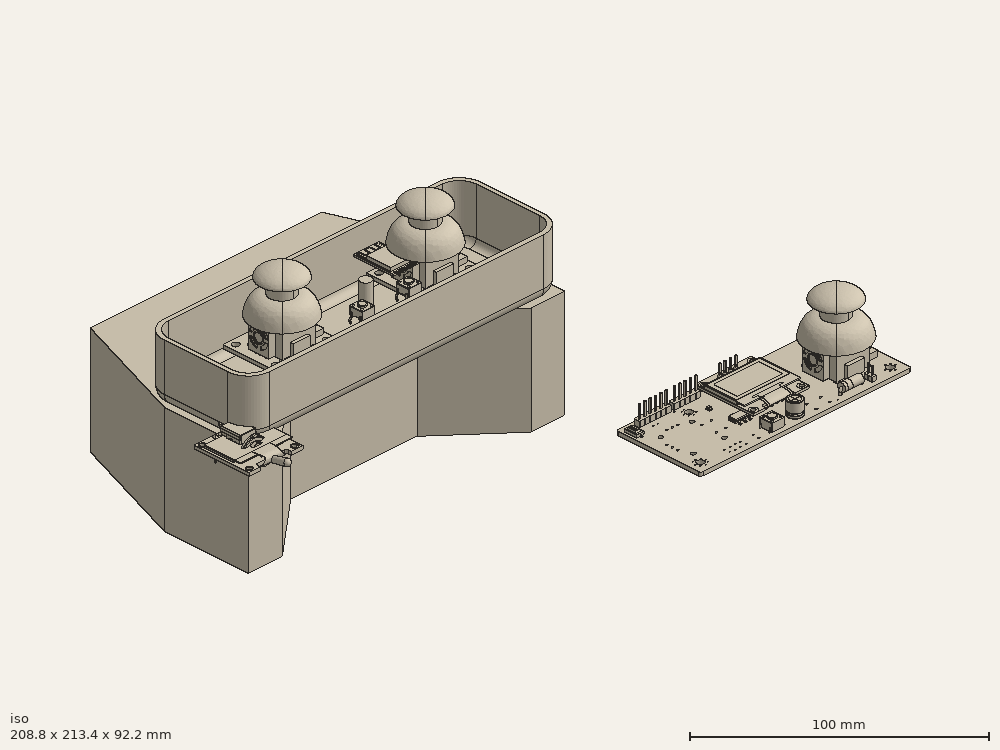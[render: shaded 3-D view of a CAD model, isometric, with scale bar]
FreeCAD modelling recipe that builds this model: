
FCSTD DOCUMENT  (FreeCAD 0.19R24366 (Git))
Label: Transmitter Case V1
License: All rights reserved
LicenseURL: http://en.wikipedia.org/wiki/All_rights_reserved
objects: Part::Feature×58, App::Link×30, Sketcher::SketchObject×13, App::Part×13, PartDesign::Pad×5, PartDesign::Body×5, PartDesign::Pocket×2, Mesh::Feature×1, PartDesign::Fillet×1, PartDesign::Thickness×1, PartDesign::CoordinateSystem×1
note: 95 computed .brp shape members not serialized (recipe doc carries the construction recipe); baked Part::Feature solids carry a one-line shape summary decoded from their .brp

FEATURE [Mesh::Feature] Xbox_One_Backplate_Electronic
  Placement = pos=(46,66,1.28e-14) rot=(1,0,0;3.14159rad)
FEATURE [Sketcher::SketchObject] Sketch
  FullyConstrained = true
  MapMode = 5
  Support = -> [XY_Plane]
  sketch-geometry (14):
    g0: LineSegment StartX=0 StartY=0 StartZ=0 EndX=0 EndY=40 EndZ=0
    g1: LineSegment StartX=0 StartY=40 StartZ=0 EndX=20 EndY=95 EndZ=0
    g2: LineSegment StartX=20 StartY=95 StartZ=0 EndX=130 EndY=95 EndZ=0
    g3: LineSegment StartX=130 StartY=95 StartZ=0 EndX=150 EndY=40 EndZ=0
    g4: LineSegment StartX=150 StartY=40 StartZ=0 EndX=150 EndY=0 EndZ=0
    g5: LineSegment StartX=150 StartY=0 StartZ=0 EndX=134 EndY=0 EndZ=0
    g6: LineSegment StartX=134 StartY=0 StartZ=0 EndX=105 EndY=25 EndZ=0
    g7: LineSegment StartX=105 StartY=25 StartZ=0 EndX=45 EndY=25 EndZ=0
    g8: LineSegment StartX=45 StartY=25 StartZ=0 EndX=16 EndY=0 EndZ=0
    g9: LineSegment StartX=16 StartY=0 StartZ=0 EndX=0 EndY=0 EndZ=0
    g10: LineSegment StartX=0 StartY=40 StartZ=0 EndX=20 EndY=40 EndZ=0
    g11: LineSegment StartX=150 StartY=40 StartZ=0 EndX=130 EndY=40 EndZ=0
    g12: LineSegment StartX=134 StartY=0 StartZ=0 EndX=105 EndY=0 EndZ=0
    g13: LineSegment StartX=16 StartY=0 StartZ=0 EndX=45 EndY=0 EndZ=0
  constraints (41):
    c: Coincident(g0,g-1)
    c: PointOnObject(g0,g-2)
    c: Coincident(g1,g0)
    c: Horizontal(g2)
    c: Coincident(g4,g3)
    c: Vertical(g4)
    c: Horizontal(g5)
    c: Coincident(g6,g5)
    c: Coincident(g7,g6)
    c: Horizontal(g7)
    c: Coincident(g8,g7)
    c: PointOnObject(g8,g-1)
    c: Coincident(g9,g8)
    c: Coincident(g9,g0)
    c: PointOnObject(g5,g-1)
    c: Equal(g0,g4)
    c: Equal(g8,g6)
    c: Equal(g9,g5)
    c: Equal(g1,g3)
    c: Coincident(g10,g0)
    c: Horizontal(g10)
    c: Coincident(g11,g3)
    c: Horizontal(g11)
    c: Coincident(g12,g5)
    c: Coincident(g13,g8)
    c: Horizontal(g13)
    c: Horizontal(g12)
    c: Vertical(g13,g7)
    c: Vertical(g12,g6)
    c: Distance(g7) = 60
    c: Distance(g3,g1) = 110
    c: Equal(g10,g11)
    c: DistanceY(g0,g2) = 95
    c: Distance(g0,g5) = 150
    c: Coincident(g1,g2)
    c: Coincident(g2,g3)
    c: Vertical(g11,g2)
    c: Coincident(g5,g4)
    c: Distance(g4) = 40
    c: Distance(g5) = 16
    c: Distance(g7,g13) = 25
FEATURE [PartDesign::Pad] Pad
  Direction = (1,1,1)
  Length = 48
  Length2 = 100
  Profile = -> Sketch
  Reversed = true
  Type = 0
FEATURE [Sketcher::SketchObject] Sketch001
  ExternalGeometry = -> [Pad]
  FullyConstrained = true
  MapMode = 5
  Support = -> [Pad]
  sketch-geometry (4):
    g0: LineSegment StartX=0 StartY=-1 StartZ=0 EndX=-63.05 EndY=-1 EndZ=0
    g1: LineSegment StartX=-63.05 StartY=-1 StartZ=0 EndX=-63.05 EndY=98.76 EndZ=0
    g2: LineSegment StartX=-63.05 StartY=98.76 StartZ=0 EndX=0 EndY=98.76 EndZ=0
    g3: LineSegment StartX=0 StartY=98.76 StartZ=0 EndX=0 EndY=-1 EndZ=0
  constraints (12):
    c: Coincident(g0,g1)
    c: Coincident(g1,g2)
    c: Coincident(g2,g3)
    c: Coincident(g3,g0)
    c: Horizontal(g0)
    c: Horizontal(g2)
    c: Vertical(g1)
    c: Vertical(g3)
    c: Distance(g0) = 63.05
    c: Distance(g3) = 99.76
    c: Vertical(g-1,g0)
    c: Distance(g-1,g0) = 1
FEATURE [PartDesign::Body] Body
  Group = -> [Sketch,Pad,Sketch001]
  Origin = -> Origin
  Tip = -> Pad
FEATURE [Sketcher::SketchObject] Sketch002
  FullyConstrained = true
  MapMode = 5
  Support = -> [XY_Plane001]
  sketch-geometry (16):
    g0: LineSegment StartX=10 StartY=0 StartZ=0 EndX=140 EndY=0 EndZ=0
    g1: LineSegment StartX=150 StartY=10 StartZ=0 EndX=150 EndY=40 EndZ=0
    g2: LineSegment StartX=140 StartY=50 StartZ=0 EndX=10 EndY=50 EndZ=0
    g3: LineSegment StartX=0 StartY=40 StartZ=0 EndX=0 EndY=10 EndZ=0
    g4: LineSegment StartX=0 StartY=0 StartZ=0 EndX=150 EndY=0 EndZ=0
    g5: LineSegment StartX=150 StartY=0 StartZ=0 EndX=150 EndY=50 EndZ=0
    g6: LineSegment StartX=150 StartY=50 StartZ=0 EndX=0 EndY=50 EndZ=0
    g7: LineSegment StartX=0 StartY=50 StartZ=0 EndX=0 EndY=0 EndZ=0
    g8: ArcOfCircle CenterX=140 CenterY=40 CenterZ=0 NormalX=0 NormalY=0 NormalZ=1 AngleXU=0 Radius=10 StartAngle=2e-16 EndAngle=1.5708
    g9: ArcOfCircle CenterX=140 CenterY=10 CenterZ=0 NormalX=0 NormalY=0 NormalZ=1 AngleXU=0 Radius=10 StartAngle=4.71239 EndAngle=6.28319
    g10: ArcOfCircle CenterX=10 CenterY=10 CenterZ=0 NormalX=0 NormalY=0 NormalZ=1 AngleXU=0 Radius=10 StartAngle=3.14159 EndAngle=4.71239
    g11: ArcOfCircle CenterX=10 CenterY=40 CenterZ=0 NormalX=0 NormalY=0 NormalZ=1 AngleXU=0 Radius=10 StartAngle=1.5708 EndAngle=3.14159
    g12: LineSegment StartX=140 StartY=40 StartZ=0 EndX=140 EndY=50 EndZ=0
    g13: LineSegment StartX=140 StartY=10 StartZ=0 EndX=140 EndY=0 EndZ=0
    g14: LineSegment StartX=10 StartY=0 StartZ=0 EndX=10 EndY=10 EndZ=0
    g15: LineSegment StartX=10 StartY=40 StartZ=0 EndX=10 EndY=50 EndZ=0
  constraints (39):
    c: Horizontal(g0)
    c: Vertical(g1)
    c: Vertical(g3)
    c: Coincident(g4,g5)
    c: Coincident(g5,g6)
    c: Coincident(g6,g7)
    c: Coincident(g7,g4)
    c: Horizontal(g4)
    c: Horizontal(g6)
    c: Vertical(g5)
    c: Vertical(g7)
    c: Coincident(g4,g-1)
    c: Distance(g5) = 50
    c: Distance(g4) = 150
    c: Tangent(g2,g8) = -1.5708
    c: Tangent(g1,g8) = -1.5708
    c: Tangent(g1,g9) = -1.5708
    c: Tangent(g0,g9) = -1.5708
    c: Tangent(g0,g10) = -1.5708
    c: Tangent(g3,g10) = -1.5708
    c: Tangent(g2,g11) = -1.5708
    c: Tangent(g3,g11) = -1.5708
    c: PointOnObject(g0,g4)
    c: PointOnObject(g3,g7)
    c: PointOnObject(g2,g6)
    c: PointOnObject(g1,g5)
    c: Coincident(g12,g8)
    c: Coincident(g12,g2)
    c: Vertical(g12)
    c: Coincident(g13,g9)
    c: Coincident(g13,g0)
    c: Coincident(g14,g0)
    c: Coincident(g14,g10)
    c: Coincident(g15,g11)
    c: Coincident(g15,g2)
    c: Equal(g15,g14)
    c: Equal(g14,g12)
    c: Equal(g12,g13)
    c: Distance(g15) = 10
FEATURE [PartDesign::Pad] Pad001
  Direction = (1,1,1)
  Length = 26
  Length2 = 100
  Profile = -> Sketch002
  Type = 0
FEATURE [PartDesign::Fillet] Fillet
  Base = -> Pad001 [Edge3]
  BaseFeature = -> Pad001
  Radius = 5
  SupportTransform = false
FEATURE [PartDesign::Thickness] Thickness
  Base = -> Fillet [Face4]
  BaseFeature = -> Fillet
  Intersection = false
  Join = 0
  Mode = 0
  Reversed = true
  SupportTransform = false
  Value = 2
FEATURE [Part::Feature] Part__Feature  label="9032"
  Placement = pos=(101,33,14) rot=(0,0,-1;1.5708rad)
  shape: bbox 56.58 x 56.58 x 34.67 mm, 175 faces (baked)
FEATURE [Part::Feature] Part__Feature001  label="9032001"
  Placement = pos=(33,33,14) rot=(0,0,-1;1.5708rad)
  shape: bbox 56.58 x 56.58 x 34.67 mm, 175 faces (baked)
FEATURE [Part::Feature] Part__Feature002  label="board"
  shape: bbox 25.4 x 26.2 x 1.51 mm, 314 faces, 9 solids (baked)
FEATURE [Part::Feature] Part__Feature003  label="screen"
  shape: bbox 24.7 x 17 x 1.8 mm, 20 faces, 3 solids (baked)
FEATURE [Part::Feature] Part__Feature004  label="pin_header"
  shape: bbox 10.16 x 2.54 x 11 mm, 112 faces, 8 solids (baked)
FEATURE [Part::Feature] Part__Feature005  label="soldering"
  shape: bbox 9.839 x 2.219 x 0.9038 mm, 24 faces, 4 solids (baked)
FEATURE [Part::Feature] Part__Feature006  label="smd_capacitor"
  Placement = pos=(10.775,1.3,0) rot=(1,0,0;3.14159rad)
  shape: bbox 0.85 x 1.6 x 0.8 mm, 18 faces, 3 solids (baked)
FEATURE [Part::Feature] Part__Feature007  label="smd_capacitor (1)"
  Placement = pos=(9.275,1.3,0) rot=(1,0,0;3.14159rad)
  shape: bbox 0.85 x 1.6 x 0.8 mm, 18 faces, 3 solids (baked)
FEATURE [Part::Feature] Part__Feature008  label="914_smd_resistor"
  Placement = pos=(7.775,1.3,0) rot=(1,0,0;3.14159rad)
  shape: bbox 0.85 x 1.55 x 0.46 mm, 76 faces, 3 solids (baked)
FEATURE [Part::Feature] Part__Feature009  label="472_smd_resistor"
  Placement = pos=(6.275,1.3,0) rot=(1,0,0;3.14159rad)
  shape: bbox 0.85 x 1.55 x 0.46 mm, 69 faces, 3 solids (baked)
FEATURE [Part::Feature] Part__Feature010  label="472_smd_resistor001"
  Placement = pos=(4.775,1.3,0) rot=(1,0,0;3.14159rad)
  shape: bbox 0.85 x 1.55 x 0.46 mm, 69 faces, 3 solids (baked)
FEATURE [Part::Feature] Part__Feature011  label="472_smd_resistor002"
  Placement = pos=(3.275,1.3,0) rot=(1,0,0;3.14159rad)
  shape: bbox 0.85 x 1.55 x 0.46 mm, 69 faces, 3 solids (baked)
FEATURE [Part::Feature] Part__Feature012  label="t4_smd_diode"
  Placement = pos=(1.375,1.3,-0.19) rot=(1,0,0;3.14159rad)
  shape: bbox 1.272 x 2.502 x 1.002 mm, 51 faces, 3 solids (baked)
FEATURE [Part::Feature] Part__Feature013  label="smd_capacitor (2)"
  Placement = pos=(-0.225,1.3,0) rot=(1,0,0;3.14159rad)
  shape: bbox 0.85 x 1.6 x 0.8 mm, 18 faces, 3 solids (baked)
FEATURE [Part::Feature] Part__Feature014  label="smd_capacitor (3)"
  Placement = pos=(-3.725,1.3,0) rot=(1,0,0;3.14159rad)
  shape: bbox 0.85 x 1.6 x 0.8 mm, 18 faces, 3 solids (baked)
FEATURE [Part::Feature] Part__Feature015  label="smd_capacitor (4)"
  Placement = pos=(-5.225,1.3,0) rot=(1,0,0;3.14159rad)
  shape: bbox 0.85 x 1.6 x 0.8 mm, 18 faces, 3 solids (baked)
FEATURE [Part::Feature] Part__Feature016  label="smd_capacitor (5)"
  Placement = pos=(-7.725,1.3,0) rot=(1,0,0;3.14159rad)
  shape: bbox 0.85 x 1.6 x 0.8 mm, 18 faces, 3 solids (baked)
FEATURE [Part::Feature] Part__Feature017  label="smd_capacitor (6)"
  Placement = pos=(-9.225,1.3,0) rot=(1,0,0;3.14159rad)
  shape: bbox 0.85 x 1.6 x 0.8 mm, 18 faces, 3 solids (baked)
FEATURE [Part::Feature] Part__Feature018  label="472_smd_resistor (1)"
  Placement = pos=(6.925,6.675,0) rot=(0.707107,-0.707107,0;3.14159rad)
  shape: bbox 1.55 x 0.85 x 0.46 mm, 69 faces, 3 solids (baked)
FEATURE [Part::Feature] Part__Feature019  label="SOT-23_XC6206 v3"
  Placement = pos=(-0.75,7.3,-0.1) rot=(0.707107,-0.707107,0;3.14159rad)
  shape: bbox 2.9 x 2.8 x 1.21 mm, 135 faces, 4 solids (baked)
FEATURE [Part::Feature] Part__Feature020  label="smd_capacitor (7)"
  Placement = pos=(-4,7.3,-0.8) rot=(0,0,1;0rad)
  shape: bbox 0.85 x 1.6 x 0.8 mm, 18 faces, 3 solids (baked)
FEATURE [Part::Feature] Part__Feature021  label="flat_cable"
  shape: bbox 22 x 8.057 x 3.352 mm, 10 faces (baked)
FEATURE [App::Part] SSD1306_OLED_Display_128x64__v23  label="SSD1306_OLED_Display(128x64) v23"
  Group = -> [Part__Feature002,Part__Feature003,Part__Feature004,Part__Feature005,Part__Feature006,Part__Feature007,Part__Feature008,Part__Feature009,Part__Feature010,Part__Feature011,Part__Feature012,Part__Feature013,Part__Feature014,Part__Feature015,Part__Feature016,Part__Feature017,Part__Feature018,Part__Feature019,Part__Feature020,Part__Feature021]
  Origin = -> Origin002
  Placement = pos=(75,30,24) rot=(0,0,1;0rad)
FEATURE [Part::Feature] Part__Feature022  label="COMPOUND"
  shape: bbox 12 x 9.988 x 12.9 mm, 195 faces, 5 solids (baked)
FEATURE [App::Part] MTS_1xx_Base_TH  label="MTS-1xx-Base_TH"
  Group = -> [Part__Feature022]
  Origin = -> Origin003
FEATURE [Part::Feature] Part__Feature024  label="MTS-1xx-Handle"
  Placement = pos=(0,-8.8,0) rot=(0,0,1;0rad)
  shape: bbox 3.8 x 17.38 x 5.93 mm, 7 faces (baked)
FEATURE [Part::Feature] Part__Feature025  label="MTS-1xx-Contact"
  Placement = pos=(0,5.9,0) rot=(0,0,1;0rad)
  shape: bbox 3.55 x 1.359 x 10.22 mm, 24 faces (baked)
FEATURE [Part::Feature] Part__Feature026  label="COMPOUND002"
  shape: bbox 3.55 x 20.58 x 3.55 mm, 13 faces, 3 solids (baked)
FEATURE [Part::Feature] Part__Feature027  label="COMPOUND003"
  shape: bbox 1.101 x 7.18 x 1.101 mm, 0 faces, 0 solids (baked)
FEATURE [App::Part] MTS_1xx_Pin  label="MTS-1xx-Pin"
  Group = -> [Part__Feature026,Part__Feature027]
  Origin = -> Origin004
  Placement = pos=(0,-7.39942,0.106156) rot=(-1,0,0;0.20944rad)
FEATURE [Part::Feature] Part__Feature028  label="MTS-1xx-Terminal1"
  Placement = pos=(0,5.9,0) rot=(0,0,1;0rad)
  shape: bbox 3.7 x 7.6 x 10.2 mm, 84 faces, 3 solids (baked)
FEATURE [Part::Feature] Part__Feature029  label="MTS-1xx-Housing"
  shape: bbox 7.9 x 10.3 x 13.2 mm, 921 faces, 2 solids (baked)
FEATURE [App::Part] MTS_1xx_X1  label="MTS-1xx-X1"
  Group = -> [MTS_1xx_Base_TH,Part__Feature024,Part__Feature025,MTS_1xx_Pin,Part__Feature028,Part__Feature029]
  Origin = -> Origin005
  Placement = pos=(16,42,17) rot=(0,0,-1;3.14159rad)
FEATURE [Part::Feature] Part__Feature030  label="MTS-1xx-Contact001"
  Placement = pos=(0,5.9,0) rot=(0,0,1;0rad)
  shape: bbox 3.55 x 1.359 x 10.22 mm, 24 faces (baked)
FEATURE [Part::Feature] Part__Feature031  label="MTS-1xx-Handle001"
  Placement = pos=(0,-8.8,0) rot=(0,0,1;0rad)
  shape: bbox 3.8 x 17.38 x 5.93 mm, 7 faces (baked)
FEATURE [Part::Feature] Part__Feature032  label="COMPOUND004"
  shape: bbox 3.55 x 20.58 x 3.55 mm, 13 faces, 3 solids (baked)
FEATURE [Part::Feature] Part__Feature033  label="COMPOUND005"
  shape: bbox 1.101 x 7.18 x 1.101 mm, 0 faces, 0 solids (baked)
FEATURE [App::Part] MTS_1xx_Pin001  label="MTS-1xx-Pin001"
  Group = -> [Part__Feature032,Part__Feature033]
  Origin = -> Origin007
  Placement = pos=(0,-7.39942,0.106156) rot=(-1,0,0;0.20944rad)
FEATURE [Part::Feature] Part__Feature034  label="COMPOUND006"
  shape: bbox 12 x 9.988 x 12.9 mm, 195 faces, 5 solids (baked)
FEATURE [App::Part] MTS_1xx_Base_TH001  label="MTS-1xx-Base_TH001"
  Group = -> [Part__Feature034]
  Origin = -> Origin008
FEATURE [Part::Feature] Part__Feature035  label="MTS-1xx-Terminal002"
  Placement = pos=(0,5.9,0) rot=(0,0,1;0rad)
  shape: bbox 3.7 x 7.6 x 10.2 mm, 84 faces, 3 solids (baked)
FEATURE [Part::Feature] Part__Feature036  label="MTS-1xx-Housing001"
  shape: bbox 7.9 x 10.3 x 13.2 mm, 921 faces, 2 solids (baked)
FEATURE [App::Part] MTS_1xx_X002  label="MTS-1xx-X002"
  Group = -> [MTS_1xx_Base_TH001,Part__Feature031,Part__Feature030,MTS_1xx_Pin001,Part__Feature035,Part__Feature036]
  Origin = -> Origin006
  Placement = pos=(134,42,17) rot=(0,0,-1;3.14159rad)
FEATURE [Part::Feature] Part__Feature037  label="Tactile Switch 6mm - THT"
  Placement = pos=(64,10,22) rot=(0,0,1;0rad)
  shape: bbox 7.902 x 6.002 x 7.802 mm, 138 faces, 7 solids (baked)
FEATURE [Sketcher::SketchObject] Sketch003
  FullyConstrained = true
  MapMode = 5
  Support = -> [XY_Plane009]
  sketch-geometry (40):
    g0: LineSegment StartX=0 StartY=0 StartZ=0 EndX=30 EndY=0 EndZ=0
    g1: LineSegment StartX=30 StartY=0 StartZ=0 EndX=30 EndY=25 EndZ=0
    g2: LineSegment StartX=30 StartY=25 StartZ=0 EndX=0 EndY=25 EndZ=0
    g3: LineSegment StartX=0 StartY=25 StartZ=0 EndX=0 EndY=0 EndZ=0
    g4: Circle CenterX=4.4 CenterY=8.5 CenterZ=0 NormalX=0 NormalY=0 NormalZ=1 AngleXU=0 Radius=0.75
    g5: Circle CenterX=4.4 CenterY=11.05 CenterZ=0 NormalX=0 NormalY=0 NormalZ=1 AngleXU=0 Radius=0.75
    g6: Circle CenterX=4.4 CenterY=13.6 CenterZ=0 NormalX=0 NormalY=0 NormalZ=1 AngleXU=0 Radius=0.75
    g7: Circle CenterX=11.4 CenterY=20.6 CenterZ=0 NormalX=0 NormalY=0 NormalZ=1 AngleXU=0 Radius=0.75
    g8: Circle CenterX=13.95 CenterY=20.6 CenterZ=0 NormalX=0 NormalY=0 NormalZ=1 AngleXU=0 Radius=0.75
    g9: Circle CenterX=16.5 CenterY=20.6 CenterZ=0 NormalX=0 NormalY=0 NormalZ=1 AngleXU=0 Radius=0.75
    g10: Circle CenterX=26.4 CenterY=14.65 CenterZ=0 NormalX=0 NormalY=0 NormalZ=1 AngleXU=0 Radius=0.75
    g11: Circle CenterX=26.4 CenterY=7.8 CenterZ=0 NormalX=0 NormalY=0 NormalZ=1 AngleXU=0 Radius=0.75
    g12: Circle CenterX=22.1 CenterY=7.8 CenterZ=0 NormalX=0 NormalY=0 NormalZ=1 AngleXU=0 Radius=0.75
    g13: Circle CenterX=22.1 CenterY=14.65 CenterZ=0 NormalX=0 NormalY=0 NormalZ=1 AngleXU=0 Radius=0.75
    g14: Circle CenterX=6.5 CenterY=3.35 CenterZ=0 NormalX=0 NormalY=0 NormalZ=1 AngleXU=0 Radius=1
    g15: Circle CenterX=6.5 CenterY=18.75 CenterZ=0 NormalX=0 NormalY=0 NormalZ=1 AngleXU=0 Radius=1
    g16: Circle CenterX=21.35 CenterY=3.35 CenterZ=0 NormalX=0 NormalY=0 NormalZ=1 AngleXU=0 Radius=1
    g17: Circle CenterX=21.35 CenterY=18.75 CenterZ=0 NormalX=0 NormalY=0 NormalZ=1 AngleXU=0 Radius=1
    g18: LineSegment StartX=13.95 StartY=20.6 StartZ=0 EndX=13.95 EndY=25 EndZ=0
    g19: LineSegment StartX=16.5 StartY=20.6 StartZ=0 EndX=13.95 EndY=20.6 EndZ=0
    g20: LineSegment StartX=11.4 StartY=20.6 StartZ=0 EndX=13.95 EndY=20.6 EndZ=0
    g21: LineSegment StartX=13.95 StartY=20.6 StartZ=0 EndX=0 EndY=20.6 EndZ=0
    g22: LineSegment StartX=4.4 StartY=11.05 StartZ=0 EndX=0 EndY=11.05 EndZ=0
    g23: LineSegment StartX=4.4 StartY=13.6 StartZ=0 EndX=4.4 EndY=11.05 EndZ=0
    g24: LineSegment StartX=4.4 StartY=11.05 StartZ=0 EndX=4.4 EndY=8.5 EndZ=0
    g25: LineSegment StartX=4.4 StartY=11.05 StartZ=0 EndX=4.4 EndY=25 EndZ=0
    g26: LineSegment StartX=6.5 StartY=3.35 StartZ=0 EndX=0 EndY=3.35 EndZ=0
    g27: LineSegment StartX=6.5 StartY=3.35 StartZ=0 EndX=6.5 EndY=0 EndZ=0
    g28: LineSegment StartX=26.4 StartY=7.8 StartZ=0 EndX=26.4 EndY=0 EndZ=0
    g29: LineSegment StartX=26.4 StartY=7.8 StartZ=0 EndX=30 EndY=7.8 EndZ=0
    g30: LineSegment StartX=6.5 StartY=18.75 StartZ=0 EndX=6.5 EndY=25 EndZ=0
    g31: LineSegment StartX=6.5 StartY=18.75 StartZ=0 EndX=0 EndY=18.75 EndZ=0
    g32: LineSegment StartX=21.35 StartY=18.75 StartZ=0 EndX=21.35 EndY=25 EndZ=0
    g33: LineSegment StartX=21.35 StartY=18.75 StartZ=0 EndX=30 EndY=18.75 EndZ=0
    g34: LineSegment StartX=21.35 StartY=3.35 StartZ=0 EndX=21.35 EndY=0 EndZ=0
    g35: LineSegment StartX=21.35 StartY=3.35 StartZ=0 EndX=30 EndY=3.35 EndZ=0
    g36: LineSegment StartX=26.4 StartY=14.65 StartZ=0 EndX=26.4 EndY=7.8 EndZ=0
    g37: LineSegment StartX=26.4 StartY=7.8 StartZ=0 EndX=22.1 EndY=7.8 EndZ=0
    g38: LineSegment StartX=22.1 StartY=14.65 StartZ=0 EndX=22.1 EndY=7.8 EndZ=0
    g39: LineSegment StartX=26.4 StartY=14.65 StartZ=0 EndX=22.1 EndY=14.65 EndZ=0
  constraints (111):
    c: Coincident(g0,g1)
    c: Coincident(g1,g2)
    c: Coincident(g2,g3)
    c: Coincident(g3,g0)
    c: Horizontal(g0)
    c: Horizontal(g2)
    c: Vertical(g1)
    c: Vertical(g3)
    c: Coincident(g0,g-1)
    c: Distance(g2) = 30
    c: Distance(g1) = 25
    c: Diameter(g4) = 1.5
    c: Equal(g4,g5) = 1.5
    c: Equal(g4,g6) = 1.5
    c: Equal(g4,g7) = 1.5
    c: Equal(g4,g8) = 1.5
    c: Equal(g4,g9) = 1.5
    c: Equal(g4,g10) = 1.5
    c: Equal(g4,g11) = 1.5
    c: Equal(g4,g12) = 1.5
    c: Diameter(g14) = 2
    c: Equal(g14,g15) = 2
    c: Equal(g14,g16) = 2
    c: Equal(g14,g17) = 2
    c: Coincident(g18,g8)
    c: Vertical(g18)
    c: Coincident(g19,g9)
    c: Coincident(g19,g8)
    c: Horizontal(g19)
    c: Coincident(g20,g7)
    c: Coincident(g20,g8)
    c: Horizontal(g20)
    c: Equal(g20,g19)
    c: Distance(g18) = 4.4
    c: Coincident(g21,g8)
    c: PointOnObject(g21,g3)
    c: Horizontal(g21)
    c: PointOnObject(g18,g2)
    c: Distance(g21) = 13.95
    c: Distance(g20) = 2.55
    c: Coincident(g22,g5)
    c: PointOnObject(g22,g-2)
    c: Horizontal(g22)
    c: Coincident(g23,g6)
    c: Coincident(g23,g5)
    c: Vertical(g23)
    c: Coincident(g24,g5)
    c: Coincident(g24,g4)
    c: Vertical(g24)
    c: Equal(g24,g23)
    c: Distance(g22) = 4.4
    c: Coincident(g25,g5)
    c: PointOnObject(g25,g2)
    c: Vertical(g25)
    c: Distance(g25) = 13.95
    c: Distance(g24) = 2.55
    c: Coincident(g26,g14)
    c: PointOnObject(g26,g-2)
    c: Horizontal(g26)
    c: Coincident(g27,g14)
    c: PointOnObject(g27,g0)
    c: Vertical(g27)
    c: Coincident(g28,g11)
    c: PointOnObject(g28,g0)
    c: Vertical(g28)
    c: Coincident(g29,g11)
    c: Horizontal(g29)
    c: Coincident(g30,g15)
    c: PointOnObject(g30,g2)
    c: Vertical(g30)
    c: Coincident(g31,g15)
    c: PointOnObject(g31,g3)
    c: Horizontal(g31)
    c: Coincident(g32,g17)
    c: PointOnObject(g32,g2)
    c: Vertical(g32)
    c: Coincident(g33,g17)
    c: PointOnObject(g33,g1)
    c: Horizontal(g33)
    c: Coincident(g34,g16)
    c: PointOnObject(g34,g0)
    c: Vertical(g34)
    c: Coincident(g35,g16)
    c: PointOnObject(g35,g1)
    c: Horizontal(g35)
    c: Coincident(g36,g10)
    c: Coincident(g36,g11)
    c: Vertical(g36)
    c: Coincident(g37,g11)
    c: Coincident(g37,g12)
    c: Horizontal(g37)
    c: Coincident(g38,g13)
    c: Coincident(g38,g12)
    c: Vertical(g38)
    c: Coincident(g39,g10)
    c: Coincident(g39,g13)
    c: Horizontal(g39)
    c: Distance(g29) = 3.6
    c: Distance(g37) = 4.3
    c: Distance(g38) = 6.85
    c: Distance(g28) = 7.8
    c: PointOnObject(g29,g1)
    c: Equal(g13,g12)
    c: Distance(g31) = 6.5
    c: Distance(g30) = 6.25
    c: Distance(g32) = 6.25
    c: Distance(g33) = 8.65
    c: Distance(g35) = 8.65
    c: Distance(g34) = 3.35
    c: Distance(g27) = 3.35
    c: Distance(g26) = 6.5
FEATURE [PartDesign::Pad] Pad002
  Direction = (1,1,1)
  Length = 1.6
  Length2 = 100
  Profile = -> Sketch003
  Type = 0
FEATURE [Sketcher::SketchObject] Sketch004
  ExternalGeometry = -> [Pad002]
  FullyConstrained = true
  MapMode = 5
  Placement = pos=(0,0,1.6) rot=(0,0,1;0rad)
  Support = -> [Pad002]
  sketch-geometry (4):
    g0: Circle CenterX=27 CenterY=22 CenterZ=0 NormalX=0 NormalY=0 NormalZ=1 AngleXU=0 Radius=1.55
    g1: Circle CenterX=3 CenterY=22 CenterZ=0 NormalX=0 NormalY=0 NormalZ=1 AngleXU=0 Radius=1.55
    g2: Circle CenterX=27 CenterY=3 CenterZ=0 NormalX=0 NormalY=0 NormalZ=1 AngleXU=0 Radius=1.55
    g3: Circle CenterX=3 CenterY=3 CenterZ=0 NormalX=0 NormalY=0 NormalZ=1 AngleXU=0 Radius=1.55
  constraints (12):
    c: Diameter(g0) = 3.1
    c: Equal(g0,g1) = 3.1
    c: Equal(g0,g2) = 3.1
    c: Equal(g0,g3) = 3.1
    c: Distance(g2,g-5) = 3
    c: Distance(g2,g-6) = 3
    c: Distance(g0,g-3) = 3
    c: Distance(g0,g-5) = 3
    c: Distance(g1,g-3) = 3
    c: Distance(g1,g-4) = 3
    c: Distance(g3,g-4) = 3
    c: Distance(g3,g-6) = 3
FEATURE [PartDesign::Pocket] Pocket
  BaseFeature = -> Pad002
  Length = 5
  Length2 = 100
  Profile = -> Sketch004
  Type = 0
FEATURE [Sketcher::SketchObject] Sketch006
  FullyConstrained = true
  MapMode = 5
  Support = -> [XY_Plane010]
  sketch-geometry (40):
    g0: LineSegment StartX=0 StartY=0 StartZ=0 EndX=30 EndY=0 EndZ=0
    g1: LineSegment StartX=30 StartY=0 StartZ=0 EndX=30 EndY=25 EndZ=0
    g2: LineSegment StartX=30 StartY=25 StartZ=0 EndX=0 EndY=25 EndZ=0
    g3: LineSegment StartX=0 StartY=25 StartZ=0 EndX=0 EndY=0 EndZ=0
    g4: Circle CenterX=4.4 CenterY=8.5 CenterZ=0 NormalX=0 NormalY=0 NormalZ=1 AngleXU=0 Radius=0.75
    g5: Circle CenterX=4.4 CenterY=11.05 CenterZ=0 NormalX=0 NormalY=0 NormalZ=1 AngleXU=0 Radius=0.75
    g6: Circle CenterX=4.4 CenterY=13.6 CenterZ=0 NormalX=0 NormalY=0 NormalZ=1 AngleXU=0 Radius=0.75
    g7: Circle CenterX=11.4 CenterY=20.6 CenterZ=0 NormalX=0 NormalY=0 NormalZ=1 AngleXU=0 Radius=0.75
    g8: Circle CenterX=13.95 CenterY=20.6 CenterZ=0 NormalX=0 NormalY=0 NormalZ=1 AngleXU=0 Radius=0.75
    g9: Circle CenterX=16.5 CenterY=20.6 CenterZ=0 NormalX=0 NormalY=0 NormalZ=1 AngleXU=0 Radius=0.75
    g10: Circle CenterX=26.4 CenterY=14.65 CenterZ=0 NormalX=0 NormalY=0 NormalZ=1 AngleXU=0 Radius=0.75
    g11: Circle CenterX=26.4 CenterY=7.8 CenterZ=0 NormalX=0 NormalY=0 NormalZ=1 AngleXU=0 Radius=0.75
    g12: Circle CenterX=22.1 CenterY=7.8 CenterZ=0 NormalX=0 NormalY=0 NormalZ=1 AngleXU=0 Radius=0.75
    g13: Circle CenterX=22.1 CenterY=14.65 CenterZ=0 NormalX=0 NormalY=0 NormalZ=1 AngleXU=0 Radius=0.75
    g14: Circle CenterX=6.5 CenterY=3.35 CenterZ=0 NormalX=0 NormalY=0 NormalZ=1 AngleXU=0 Radius=1
    g15: Circle CenterX=6.5 CenterY=18.75 CenterZ=0 NormalX=0 NormalY=0 NormalZ=1 AngleXU=0 Radius=1
    g16: Circle CenterX=21.35 CenterY=3.35 CenterZ=0 NormalX=0 NormalY=0 NormalZ=1 AngleXU=0 Radius=1
    g17: Circle CenterX=21.35 CenterY=18.75 CenterZ=0 NormalX=0 NormalY=0 NormalZ=1 AngleXU=0 Radius=1
    g18: LineSegment StartX=13.95 StartY=20.6 StartZ=0 EndX=13.95 EndY=25 EndZ=0
    g19: LineSegment StartX=16.5 StartY=20.6 StartZ=0 EndX=13.95 EndY=20.6 EndZ=0
    g20: LineSegment StartX=11.4 StartY=20.6 StartZ=0 EndX=13.95 EndY=20.6 EndZ=0
    g21: LineSegment StartX=13.95 StartY=20.6 StartZ=0 EndX=0 EndY=20.6 EndZ=0
    g22: LineSegment StartX=4.4 StartY=11.05 StartZ=0 EndX=0 EndY=11.05 EndZ=0
    g23: LineSegment StartX=4.4 StartY=13.6 StartZ=0 EndX=4.4 EndY=11.05 EndZ=0
    g24: LineSegment StartX=4.4 StartY=11.05 StartZ=0 EndX=4.4 EndY=8.5 EndZ=0
    g25: LineSegment StartX=4.4 StartY=11.05 StartZ=0 EndX=4.4 EndY=25 EndZ=0
    g26: LineSegment StartX=6.5 StartY=3.35 StartZ=0 EndX=0 EndY=3.35 EndZ=0
    g27: LineSegment StartX=6.5 StartY=3.35 StartZ=0 EndX=6.5 EndY=0 EndZ=0
    g28: LineSegment StartX=26.4 StartY=7.8 StartZ=0 EndX=26.4 EndY=0 EndZ=0
    g29: LineSegment StartX=26.4 StartY=7.8 StartZ=0 EndX=30 EndY=7.8 EndZ=0
    g30: LineSegment StartX=6.5 StartY=18.75 StartZ=0 EndX=6.5 EndY=25 EndZ=0
    g31: LineSegment StartX=6.5 StartY=18.75 StartZ=0 EndX=0 EndY=18.75 EndZ=0
    g32: LineSegment StartX=21.35 StartY=18.75 StartZ=0 EndX=21.35 EndY=25 EndZ=0
    g33: LineSegment StartX=21.35 StartY=18.75 StartZ=0 EndX=30 EndY=18.75 EndZ=0
    g34: LineSegment StartX=21.35 StartY=3.35 StartZ=0 EndX=21.35 EndY=0 EndZ=0
    g35: LineSegment StartX=21.35 StartY=3.35 StartZ=0 EndX=30 EndY=3.35 EndZ=0
    g36: LineSegment StartX=26.4 StartY=14.65 StartZ=0 EndX=26.4 EndY=7.8 EndZ=0
    g37: LineSegment StartX=26.4 StartY=7.8 StartZ=0 EndX=22.1 EndY=7.8 EndZ=0
    g38: LineSegment StartX=22.1 StartY=14.65 StartZ=0 EndX=22.1 EndY=7.8 EndZ=0
    g39: LineSegment StartX=26.4 StartY=14.65 StartZ=0 EndX=22.1 EndY=14.65 EndZ=0
  constraints (111):
    c: Coincident(g0,g1)
    c: Coincident(g1,g2)
    c: Coincident(g2,g3)
    c: Coincident(g3,g0)
    c: Horizontal(g0)
    c: Horizontal(g2)
    c: Vertical(g1)
    c: Vertical(g3)
    c: Coincident(g0,g-1)
    c: Distance(g2) = 30
    c: Distance(g1) = 25
    c: Diameter(g4) = 1.5
    c: Equal(g4,g5) = 1.5
    c: Equal(g4,g6) = 1.5
    c: Equal(g4,g7) = 1.5
    c: Equal(g4,g8) = 1.5
    c: Equal(g4,g9) = 1.5
    c: Equal(g4,g10) = 1.5
    c: Equal(g4,g11) = 1.5
    c: Equal(g4,g12) = 1.5
    c: Diameter(g14) = 2
    c: Equal(g14,g15) = 2
    c: Equal(g14,g16) = 2
    c: Equal(g14,g17) = 2
    c: Coincident(g18,g8)
    c: Vertical(g18)
    c: Coincident(g19,g9)
    c: Coincident(g19,g8)
    c: Horizontal(g19)
    c: Coincident(g20,g7)
    c: Coincident(g20,g8)
    c: Horizontal(g20)
    c: Equal(g20,g19)
    c: Distance(g18) = 4.4
    c: Coincident(g21,g8)
    c: PointOnObject(g21,g3)
    c: Horizontal(g21)
    c: PointOnObject(g18,g2)
    c: Distance(g21) = 13.95
    c: Distance(g20) = 2.55
    c: Coincident(g22,g5)
    c: PointOnObject(g22,g-2)
    c: Horizontal(g22)
    c: Coincident(g23,g6)
    c: Coincident(g23,g5)
    c: Vertical(g23)
    c: Coincident(g24,g5)
    c: Coincident(g24,g4)
    c: Vertical(g24)
    c: Equal(g24,g23)
    c: Distance(g22) = 4.4
    c: Coincident(g25,g5)
    c: PointOnObject(g25,g2)
    c: Vertical(g25)
    c: Distance(g25) = 13.95
    c: Distance(g24) = 2.55
    c: Coincident(g26,g14)
    c: PointOnObject(g26,g-2)
    c: Horizontal(g26)
    c: Coincident(g27,g14)
    c: PointOnObject(g27,g0)
    c: Vertical(g27)
    c: Coincident(g28,g11)
    c: PointOnObject(g28,g0)
    c: Vertical(g28)
    c: Coincident(g29,g11)
    c: Horizontal(g29)
    c: Coincident(g30,g15)
    c: PointOnObject(g30,g2)
    c: Vertical(g30)
    c: Coincident(g31,g15)
    c: PointOnObject(g31,g3)
    c: Horizontal(g31)
    c: Coincident(g32,g17)
    c: PointOnObject(g32,g2)
    c: Vertical(g32)
    c: Coincident(g33,g17)
    c: PointOnObject(g33,g1)
    c: Horizontal(g33)
    c: Coincident(g34,g16)
    c: PointOnObject(g34,g0)
    c: Vertical(g34)
    c: Coincident(g35,g16)
    c: PointOnObject(g35,g1)
    c: Horizontal(g35)
    c: Coincident(g36,g10)
    c: Coincident(g36,g11)
    c: Vertical(g36)
    c: Coincident(g37,g11)
    c: Coincident(g37,g12)
    c: Horizontal(g37)
    c: Coincident(g38,g13)
    c: Coincident(g38,g12)
    c: Vertical(g38)
    c: Coincident(g39,g10)
    c: Coincident(g39,g13)
    c: Horizontal(g39)
    c: Distance(g29) = 3.6
    c: Distance(g37) = 4.3
    c: Distance(g38) = 6.85
    c: Distance(g28) = 7.8
    c: PointOnObject(g29,g1)
    c: Equal(g13,g12)
    c: Distance(g31) = 6.5
    c: Distance(g30) = 6.25
    c: Distance(g32) = 6.25
    c: Distance(g33) = 8.65
    c: Distance(g35) = 8.65
    c: Distance(g34) = 3.35
    c: Distance(g27) = 3.35
    c: Distance(g26) = 6.5
FEATURE [PartDesign::Pad] Pad003
  Direction = (1,1,1)
  Length = 1.6
  Length2 = 100
  Profile = -> Sketch006
  Type = 0
FEATURE [Sketcher::SketchObject] Sketch005
  ExternalGeometry = -> [Pad003]
  FullyConstrained = true
  MapMode = 5
  Placement = pos=(0,0,1.6) rot=(0,0,1;0rad)
  Support = -> [Pad003]
  sketch-geometry (4):
    g0: Circle CenterX=27 CenterY=22 CenterZ=0 NormalX=0 NormalY=0 NormalZ=1 AngleXU=0 Radius=1.55
    g1: Circle CenterX=3 CenterY=22 CenterZ=0 NormalX=0 NormalY=0 NormalZ=1 AngleXU=0 Radius=1.55
    g2: Circle CenterX=27 CenterY=3 CenterZ=0 NormalX=0 NormalY=0 NormalZ=1 AngleXU=0 Radius=1.55
    g3: Circle CenterX=3 CenterY=3 CenterZ=0 NormalX=0 NormalY=0 NormalZ=1 AngleXU=0 Radius=1.55
  constraints (12):
    c: Diameter(g0) = 3.1
    c: Equal(g0,g1) = 3.1
    c: Equal(g0,g2) = 3.1
    c: Equal(g0,g3) = 3.1
    c: Distance(g2,g-5) = 3
    c: Distance(g2,g-6) = 3
    c: Distance(g0,g-3) = 3
    c: Distance(g0,g-5) = 3
    c: Distance(g1,g-3) = 3
    c: Distance(g1,g-4) = 3
    c: Distance(g3,g-4) = 3
    c: Distance(g3,g-6) = 3
FEATURE [PartDesign::Pocket] Pocket001
  BaseFeature = -> Pad003
  Length = 5
  Length2 = 100
  Profile = -> Sketch005
  Type = 0
FEATURE [PartDesign::Body] Body003
  Group = -> [Sketch006,Pad003,Sketch005,Pocket001]
  Origin = -> Origin010
  Placement = pos=(95,14,12) rot=(0,0,1;0rad)
  Tip = -> Pocket001
FEATURE [Part::Feature] Part__Feature039  label="Tactile Switch 6mm - THT002"
  Placement = pos=(86,10,22) rot=(0,0,1;0rad)
  shape: bbox 7.902 x 6.002 x 7.802 mm, 138 faces, 7 solids (baked)
FEATURE [Sketcher::SketchObject] Sketch007
  FullyConstrained = true
  MapMode = 5
  Support = -> [XY_Plane011]
  sketch-geometry (38):
    g0: LineSegment StartX=0 StartY=0 StartZ=0 EndX=150 EndY=0 EndZ=0
    g1: LineSegment StartX=150 StartY=0 StartZ=0 EndX=150 EndY=50 EndZ=0
    g2: LineSegment StartX=150 StartY=50 StartZ=0 EndX=0 EndY=50 EndZ=0
    g3: LineSegment StartX=0 StartY=50 StartZ=0 EndX=0 EndY=0 EndZ=0
    g4: LineSegment StartX=0 StartY=0 StartZ=0 EndX=41 EndY=0 EndZ=0
    g5: LineSegment StartX=41 StartY=0 StartZ=0 EndX=41 EndY=25 EndZ=0
    g6: LineSegment StartX=41 StartY=25 StartZ=0 EndX=0 EndY=25 EndZ=0
    g7: LineSegment StartX=0 StartY=25 StartZ=0 EndX=0 EndY=0 EndZ=0
    g8: LineSegment StartX=150 StartY=0 StartZ=0 EndX=109 EndY=0 EndZ=0
    g9: LineSegment StartX=109 StartY=0 StartZ=0 EndX=109 EndY=25 EndZ=0
    g10: LineSegment StartX=109 StartY=25 StartZ=0 EndX=150 EndY=25 EndZ=0
    g11: LineSegment StartX=150 StartY=25 StartZ=0 EndX=150 EndY=0 EndZ=0
    g12: GeomPoint X=41 Y=25 Z=0
    g13: GeomPoint X=109 Y=25 Z=0
    g14: Circle CenterX=41 CenterY=25 CenterZ=0 NormalX=0 NormalY=0 NormalZ=1 AngleXU=0 Radius=10
    g15: Circle CenterX=109 CenterY=25 CenterZ=0 NormalX=0 NormalY=0 NormalZ=1 AngleXU=0 Radius=10
    g16: LineSegment StartX=75 StartY=50 StartZ=0 EndX=75 EndY=0 EndZ=0
    g17: LineSegment StartX=61 StartY=13 StartZ=0 EndX=67 EndY=13 EndZ=0
    g18: LineSegment StartX=67 StartY=13 StartZ=0 EndX=67 EndY=7 EndZ=0
    g19: LineSegment StartX=67 StartY=7 StartZ=0 EndX=61 EndY=7 EndZ=0
    g20: LineSegment StartX=61 StartY=7 StartZ=0 EndX=61 EndY=13 EndZ=0
    g21: LineSegment StartX=83 StartY=13 StartZ=0 EndX=89 EndY=13 EndZ=0
    g22: LineSegment StartX=89 StartY=13 StartZ=0 EndX=89 EndY=7 EndZ=0
    g23: LineSegment StartX=89 StartY=7 StartZ=0 EndX=83 EndY=7 EndZ=0
    g24: LineSegment StartX=83 StartY=7 StartZ=0 EndX=83 EndY=13 EndZ=0
    g25: LineSegment StartX=67 StartY=7 StartZ=0 EndX=67 EndY=0 EndZ=0
    g26: LineSegment StartX=67 StartY=7 StartZ=0 EndX=75 EndY=7 EndZ=0
    g27: LineSegment StartX=83 StartY=7 StartZ=0 EndX=75 EndY=7 EndZ=0
    g28: LineSegment StartX=83 StartY=7 StartZ=0 EndX=83 EndY=0 EndZ=0
    g29: LineSegment StartX=69.92 StartY=43 StartZ=0 EndX=80.08 EndY=43 EndZ=0
    g30: LineSegment StartX=80.08 StartY=43 StartZ=0 EndX=80.08 EndY=40.46 EndZ=0
    g31: LineSegment StartX=80.08 StartY=40.46 StartZ=0 EndX=69.92 EndY=40.46 EndZ=0
    g32: LineSegment StartX=69.92 StartY=40.46 StartZ=0 EndX=69.92 EndY=43 EndZ=0
    g33: LineSegment StartX=80.08 StartY=43 StartZ=0 EndX=80.08 EndY=50 EndZ=0
    g34: LineSegment StartX=25 StartY=50 StartZ=0 EndX=25 EndY=0 EndZ=0
    g35: LineSegment StartX=125 StartY=50 StartZ=0 EndX=125 EndY=0 EndZ=0
    g36: LineSegment StartX=25 StartY=45 StartZ=0 EndX=125 EndY=45 EndZ=0
    g37: LineSegment StartX=25 StartY=5 StartZ=0 EndX=125 EndY=5 EndZ=0
  constraints (113):
    c: Coincident(g0,g1)
    c: Coincident(g1,g2)
    c: Coincident(g2,g3)
    c: Coincident(g3,g0)
    c: Horizontal(g0)
    c: Horizontal(g2)
    c: Vertical(g1)
    c: Vertical(g3)
    c: Coincident(g0,g-1)
    c: Distance(g2) = 150
    c: Distance(g1) = 50
    c: Coincident(g4,g5)
    c: Coincident(g5,g6)
    c: Coincident(g6,g7)
    c: Coincident(g7,g4)
    c: Horizontal(g4)
    c: Horizontal(g6)
    c: Vertical(g5)
    c: Vertical(g7)
    c: Coincident(g4,g0)
    c: Coincident(g8,g9)
    c: Coincident(g9,g10)
    c: Coincident(g10,g11)
    c: Coincident(g11,g8)
    c: Horizontal(g8)
    c: Horizontal(g10)
    c: Vertical(g9)
    c: Vertical(g11)
    c: Coincident(g8,g0)
    c: Distance(g10) = 41
    c: Distance(g9) = 25
    c: Distance(g6) = 41
    c: Distance(g5) = 25
    c: Coincident(g12,g5)
    c: Coincident(g13,g9)
    c: Coincident(g14,g5)
    c: Coincident(g15,g9)
    c: Diameter(g14) = 20
    c: Diameter(g15) = 20
    c: PointOnObject(g16,g2)
    c: PointOnObject(g16,g0)
    c: Vertical(g16)
    c: Distance(g1,g16) = 75
    c: Distance(g16,g2) = 75
    c: Coincident(g17,g18)
    c: Coincident(g18,g19)
    c: Coincident(g19,g20)
    c: Coincident(g20,g17)
    c: Horizontal(g17)
    c: Horizontal(g19)
    c: Vertical(g18)
    c: Vertical(g20)
    c: Coincident(g21,g22)
    c: Coincident(g22,g23)
    c: Coincident(g23,g24)
    c: Coincident(g24,g21)
    c: Horizontal(g21)
    c: Horizontal(g23)
    c: Vertical(g22)
    c: Vertical(g24)
    c: Distance(g22) = 6
    c: Equal(g21,g22)
    c: Equal(g17,g18)
    c: Equal(g18,g21)
    c: Coincident(g25,g18)
    c: PointOnObject(g25,g0)
    c: Vertical(g25)
    c: Coincident(g26,g18)
    c: PointOnObject(g26,g16)
    c: Horizontal(g26)
    c: Coincident(g27,g23)
    c: Coincident(g27,g26)
    c: Horizontal(g27)
    c: Coincident(g28,g23)
    c: PointOnObject(g28,g0)
    c: Vertical(g28)
    c: Equal(g27,g26)
    c: Distance(g27) = 8
    c: Distance(g28) = 7
    c: Coincident(g29,g30)
    c: Coincident(g30,g31)
    c: Coincident(g31,g32)
    c: Coincident(g32,g29)
    c: Horizontal(g29)
    c: Horizontal(g31)
    c: Vertical(g30)
    c: Vertical(g32)
    c: Distance(g29) = 10.16
    c: Distance(g31,g16) = 5.08
    c: Distance(g30) = 2.54
    c: Coincident(g33,g29)
    c: PointOnObject(g33,g2)
    c: Vertical(g33)
    c: Distance(g33) = 7
    c: PointOnObject(g34,g2)
    c: PointOnObject(g34,g0)
    c: Vertical(g34)
    c: PointOnObject(g35,g2)
    c: PointOnObject(g35,g0)
    c: Vertical(g35)
    c: Distance(g35,g0) = 25
    c: Distance(g34,g0) = 25
    c: Distance(g34,g35) = 100
    c: Distance(g14,g15) = 68
    c: PointOnObject(g36,g34)
    c: PointOnObject(g36,g35)
    c: Horizontal(g36)
    c: PointOnObject(g37,g34)
    c: Horizontal(g37)
    c: PointOnObject(g37,g35)
    c: Distance(g37,g35) = 5
    c: Distance(g36,g35) = 5
    c: Distance(g36,g37) = 40
FEATURE [PartDesign::Body] Body004
  Group = -> [Sketch007]
  Origin = -> Origin011
  Placement = pos=(0,0,94) rot=(0,0,1;0rad)
FEATURE [Sketcher::SketchObject] Sketch008
  FullyConstrained = true
  MapMode = 5
  Support = -> [XY_Plane009]
FEATURE [Sketcher::SketchObject] Sketch009
  FullyConstrained = true
  MapMode = 5
  Support = -> [XY_Plane009]
FEATURE [PartDesign::Body] Body002
  Group = -> [Sketch003,Pad002,Sketch004,Pocket,Sketch008,Sketch009]
  Origin = -> Origin009
  Placement = pos=(27,14,12) rot=(0,0,1;0rad)
  Tip = -> Pocket
FEATURE [Part::Feature] Part__Feature041  label="NRF24 v7"
  Placement = pos=(80,28,23) rot=(0,0.707107,0.707107;3.14159rad)
  shape: bbox 12 x 19.01 x 2.3 mm, 136 faces (baked)
FEATURE [PartDesign::CoordinateSystem] Local_CS_4c2a
  AttacherType = Attacher::AttachEngine3D
FEATURE [Part::Feature] Pcb_4c2a
  shape: bbox 99.99 x 40.22 x 1.6 mm, 137 faces (baked)
FEATURE [Sketcher::SketchObject] PCB_Sketch_4c2a
  FullyConstrained = false
  sketch-geometry (8):
    g0: LineSegment StartX=97.155 StartY=-78.1884 StartZ=0 EndX=195.116 EndY=-78.1884 EndZ=0
    g1: LineSegment StartX=96.139 StartY=-117.392 StartZ=0 EndX=96.139 EndY=-79.2044 EndZ=0
    g2: LineSegment StartX=196.132 StartY=-79.2044 StartZ=0 EndX=196.132 EndY=-117.392 EndZ=0
    g3: LineSegment StartX=195.116 StartY=-118.408 StartZ=0 EndX=97.155 EndY=-118.408 EndZ=0
    g4: ArcOfCircle CenterX=97.155 CenterY=-117.392 CenterZ=0 NormalX=0 NormalY=0 NormalZ=-1 AngleXU=-1.57079 Radius=1.016 StartAngle=0 EndAngle=1.57079
    g5: ArcOfCircle CenterX=97.155 CenterY=-79.2044 CenterZ=0 NormalX=0 NormalY=0 NormalZ=-1 AngleXU=1.64556e-06 Radius=1.016 StartAngle=0 EndAngle=1.57079
    g6: ArcOfCircle CenterX=195.116 CenterY=-117.392 CenterZ=0 NormalX=0 NormalY=0 NormalZ=-1 AngleXU=-3.14159 Radius=1.016 StartAngle=0 EndAngle=1.57079
    g7: ArcOfCircle CenterX=195.116 CenterY=-79.2044 CenterZ=0 NormalX=0 NormalY=0 NormalZ=-1 AngleXU=1.5708 Radius=1.016 StartAngle=0 EndAngle=1.57079
  constraints (8):
    c: Coincident(g1,g4)
    c: Coincident(g1,g5)
    c: Coincident(g3,g4)
    c: Coincident(g0,g5)
    c: Coincident(g3,g6)
    c: Coincident(g0,g7)
    c: Coincident(g2,g6)
    c: Coincident(g2,g7)
FEATURE [App::Part] Board_Geoms_4c2a
  Group = -> [Local_CS_4c2a,Pcb_4c2a,PCB_Sketch_4c2a]
  Origin = -> Origin013
  Placement = pos=(-96.12,118.42,0) rot=(0,0,1;0rad)
FEATURE [Part::Feature] Shape  label="R4_R_0805_2012Metric_86a6360c6716"
  Placement = pos=(140.224,-84.582,0) rot=(0,0,1;0rad)
  shape: bbox 2 x 1.2 x 0.45 mm, 26 faces (baked)
FEATURE [Part::Feature] Shape001  label="D2_LED_0805_2012Metric_1bfca75f96b9"
  Placement = pos=(128.016,-90.433,0) rot=(0,0,-1;1.5708rad)
  shape: bbox 1.25 x 2 x 1.1 mm, 50 faces (baked)
FEATURE [Part::Feature] Shape002  label="C12_C_0805_2012Metric_d3958f6a5853"
  Placement = pos=(151.108,-100.584,0) rot=(0,0,1;3.14159rad)
  shape: bbox 2 x 1.25 x 1.25 mm, 28 faces (baked)
FEATURE [Part::Feature] Shape003  label="D1_D_5W_P10.16mm_Horizontal_74f6fe64555e"
  Placement = pos=(166.37,-114.3,0) rot=(0,0,1;0rad)
  shape: bbox 11.53 x 3.72 x 6.71 mm, 13 faces (baked)
FEATURE [App::Link] C12_C_0805_2012Metric_d3958f6a5853_ln_  label="C8_C_0805_2012Metric_02092405bc03"
  LinkPlacement = pos=(138.176,-100.584,0) rot=(0,0,1;3.14159rad)
  LinkedObject = -> Shape002
  Placement = pos=(138.176,-100.584,0) rot=(0,0,1;3.14159rad)
FEATURE [Part::Feature] Shape004  label="SW7_9032_e1245dbca964"
  Placement = pos=(171.086,-91.798,0) rot=(0,0,-1;1.5708rad)
  shape: bbox 56.58 x 56.58 x 34.67 mm, 175 faces (baked)
FEATURE [Part::Feature] Shape005  label="SW3_SW_PUSH_6mm_3aecc2847bb8"
  Placement = pos=(131.878,-111.034,0) rot=(0,0,1;0rad)
  shape: bbox 7.174 x 6 x 7.8 mm, 105 faces (baked)
FEATURE [App::Link] D2_LED_0805_2012Metric_1bfca75f96b9_ln_  label="D4_LED_0805_2012Metric_4bae967a934e"
  LinkPlacement = pos=(130.556,-86.369,0) rot=(0,0,-1;1.5708rad)
  LinkedObject = -> Shape001
  Placement = pos=(130.556,-86.369,0) rot=(0,0,-1;1.5708rad)
FEATURE [Part::Feature] Shape006  label="C1_CP_Radial_D63mm_P250mm_e02b7d5e331a"
  Placement = pos=(146.05,-114.466,0) rot=(0,0,1;1.5708rad)
  shape: bbox 8.053 x 7.785 x 8.3 mm, 46 faces (baked)
FEATURE [App::Link] C12_C_0805_2012Metric_d3958f6a5853_ln_001  label="C14_C_0805_2012Metric_3b0bbbb12884"
  LinkPlacement = pos=(135.89,-94.234,0) rot=(0,0,1;1.5708rad)
  LinkedObject = -> Shape002
  Placement = pos=(135.89,-94.234,0) rot=(0,0,1;1.5708rad)
FEATURE [App::Link] C12_C_0805_2012Metric_d3958f6a5853_ln_002  label="C4_C_0805_2012Metric_81c6340abaee"
  LinkPlacement = pos=(146.536,-93.98,0) rot=(0,0,1;3.14159rad)
  LinkedObject = -> Shape002
  Placement = pos=(146.536,-93.98,0) rot=(0,0,1;3.14159rad)
FEATURE [App::Link] C12_C_0805_2012Metric_d3958f6a5853_ln_003  label="C2_C_0805_2012Metric_54f9ee2013ba"
  LinkPlacement = pos=(129.561,-107.696,0) rot=(0,0,1;3.14159rad)
  LinkedObject = -> Shape002
  Placement = pos=(129.561,-107.696,0) rot=(0,0,1;3.14159rad)
FEATURE [Part::Feature] Shape007  label="U1_SOT_223_77e6ee85f18e"
  Placement = pos=(130.81,-101.854,0) rot=(0,0,1;1.5708rad)
  shape: bbox 6.5 x 7 x 1.7 mm, 78 faces (baked)
FEATURE [App::Link] R4_R_0805_2012Metric_86a6360c6716_ln_  label="R6_R_0805_2012Metric_452a967ca0c3"
  LinkPlacement = pos=(132.842,-86.344,0) rot=(0,0,-1;1.5708rad)
  LinkedObject = -> Shape
  Placement = pos=(132.842,-86.344,0) rot=(0,0,-1;1.5708rad)
FEATURE [Part::Feature] Shape008  label="SW1_SW_SPST_CK_RS282G05A3_4cddf65b1361"
  Placement = pos=(99.06,-83.82,0) rot=(0,0,-1;1.5708rad)
  shape: bbox 3.5 x 8 x 2.5 mm, 109 faces (baked)
FEATURE [App::Link] D2_LED_0805_2012Metric_1bfca75f96b9_ln_001  label="D3_LED_0805_2012Metric_e5670b9002ad"
  LinkPlacement = pos=(130.556,-90.424,0) rot=(0,0,-1;1.5708rad)
  LinkedObject = -> Shape001
  Placement = pos=(130.556,-90.424,0) rot=(0,0,-1;1.5708rad)
FEATURE [App::Link] R4_R_0805_2012Metric_86a6360c6716_ln_001  label="R14_R_0805_2012Metric_defe1b20c7a3"
  LinkPlacement = pos=(155.448,-82.82,0) rot=(0,0,-1;1.5708rad)
  LinkedObject = -> Shape
  Placement = pos=(155.448,-82.82,0) rot=(0,0,-1;1.5708rad)
FEATURE [App::Link] SW3_SW_PUSH_6mm_3aecc2847bb8_ln_  label="SW2_SW_PUSH_6mm_dcd5a8308b13"
  LinkPlacement = pos=(153.849,-111.034,0) rot=(0,0,1;0rad)
  LinkedObject = -> Shape005
  Placement = pos=(153.849,-111.034,0) rot=(0,0,1;0rad)
FEATURE [Part::Feature] Shape009  label="J2_PinHeader_1x04_P254mm_Vertical_6093e80eb8df"
  Placement = pos=(142.24,-81.28,0) rot=(0,0,1;1.5708rad)
  shape: bbox 10.16 x 2.54 x 11.54 mm, 100 faces (baked)
FEATURE [Part::Feature] Shape010  label="J2_(Unsaved)_6093e80eb8df[2]"
  Placement = pos=(180.34,-88.53,3.5) rot=(0,0,1;0rad)
  shape: bbox 26.71 x 27.87 x 10.86 mm, 219 faces, 8 solids (baked)
FEATURE [App::Link] C12_C_0805_2012Metric_d3958f6a5853_ln_004  label="C7_C_0805_2012Metric_0bbddcd65155"
  LinkPlacement = pos=(138.176,-98.044,0) rot=(0,0,1;3.14159rad)
  LinkedObject = -> Shape002
  Placement = pos=(138.176,-98.044,0) rot=(0,0,1;3.14159rad)
FEATURE [App::Link] C1_CP_Radial_D63mm_P250mm_e02b7d5e331a_ln_  label="C11_CP_Radial_D63mm_P250mm_dd6f5d560331"
  LinkPlacement = pos=(126.492,-113.118,0) rot=(0,0,-1;1.5708rad)
  LinkedObject = -> Shape006
  Placement = pos=(126.492,-113.118,0) rot=(0,0,-1;1.5708rad)
FEATURE [Part::Feature] Shape011  label="J4_PinHeader_1x06_P254mm_Vertical_f13ea3681248"
  Placement = pos=(104.14,-81.28,0) rot=(0,0,1;1.5708rad)
  shape: bbox 15.24 x 2.54 x 11.54 mm, 148 faces (baked)
FEATURE [Part::Feature] Shape012  label="J3_PinHeader_1x05_P254mm_Vertical_dfba2d34b850"
  Placement = pos=(120.655,-81.28,0) rot=(0,0,1;1.5708rad)
  shape: bbox 12.7 x 2.54 x 11.54 mm, 124 faces (baked)
FEATURE [App::Link] R4_R_0805_2012Metric_86a6360c6716_ln_002  label="R5_R_0805_2012Metric_6318803272ce"
  LinkPlacement = pos=(132.842,-90.44,0) rot=(0,0,-1;1.5708rad)
  LinkedObject = -> Shape
  Placement = pos=(132.842,-90.44,0) rot=(0,0,-1;1.5708rad)
FEATURE [App::Link] R4_R_0805_2012Metric_86a6360c6716_ln_003  label="R9_R_0805_2012Metric_f2a940b0df93"
  LinkPlacement = pos=(141.224,-111.236,0) rot=(0,0,-1;1.5708rad)
  LinkedObject = -> Shape
  Placement = pos=(141.224,-111.236,0) rot=(0,0,-1;1.5708rad)
FEATURE [App::Link] C12_C_0805_2012Metric_d3958f6a5853_ln_005  label="C3_C_0805_2012Metric_ca77ae6b8ef4"
  LinkPlacement = pos=(146.558,-96.52,0) rot=(0,0,1;3.14159rad)
  LinkedObject = -> Shape002
  Placement = pos=(146.558,-96.52,0) rot=(0,0,1;3.14159rad)
FEATURE [App::Link] C12_C_0805_2012Metric_d3958f6a5853_ln_006  label="C13_C_0805_2012Metric_eaffed6cfb20"
  LinkPlacement = pos=(130.556,-94.488,0) rot=(0,0,1;1.5708rad)
  LinkedObject = -> Shape002
  Placement = pos=(130.556,-94.488,0) rot=(0,0,1;1.5708rad)
FEATURE [App::Link] R4_R_0805_2012Metric_86a6360c6716_ln_004  label="R3_R_0805_2012Metric_17a8b9b5c5af"
  LinkPlacement = pos=(128.016,-94.504,0) rot=(0,0,1;1.5708rad)
  LinkedObject = -> Shape
  Placement = pos=(128.016,-94.504,0) rot=(0,0,1;1.5708rad)
FEATURE [App::Link] R4_R_0805_2012Metric_86a6360c6716_ln_005  label="R13_R_0805_2012Metric_f202dd2cf169"
  LinkPlacement = pos=(152.908,-82.804,0) rot=(0,0,-1;1.5708rad)
  LinkedObject = -> Shape
  Placement = pos=(152.908,-82.804,0) rot=(0,0,-1;1.5708rad)
FEATURE [App::Link] SW7_9032_e1245dbca964_ln_  label="SW6_9032_72fd94b36555"
  LinkPlacement = pos=(103.014,-91.798,0) rot=(0,0,-1;1.5708rad)
  LinkedObject = -> Shape004
  Placement = pos=(103.014,-91.798,0) rot=(0,0,-1;1.5708rad)
FEATURE [Part::Feature] Shape013  label="J1_PinHeader_1x02_P200mm_Vertical_e800824e538c"
  Placement = pos=(180.594,-113.284,0) rot=(0,0,1;0rad)
  shape: bbox 2 x 4 x 8.8 mm, 52 faces (baked)
FEATURE [App::Part] Top_4c2a
  Group = -> [Shape,Shape001,Shape002,Shape003,C12_C_0805_2012Metric_d3958f6a5853_ln_,Shape004,Shape005,D2_LED_0805_2012Metric_1bfca75f96b9_ln_,Shape006,C12_C_0805_2012Metric_d3958f6a5853_ln_001,C12_C_0805_2012Metric_d3958f6a5853_ln_002,C12_C_0805_2012Metric_d3958f6a5853_ln_003,Shape007,R4_R_0805_2012Metric_86a6360c6716_ln_,Shape008,D2_LED_0805_2012Metric_1bfca75f96b9_ln_001,+16 more]
  Origin = -> Origin015
FEATURE [App::Link] C12_C_0805_2012Metric_d3958f6a5853_ln_007  label="C10_C_0805_2012Metric_bc52b973029d"
  LinkPlacement = pos=(134.62,-113.263,-1.6) rot=(0.707107,-0.707107,0;3.14159rad)
  LinkedObject = -> Shape002
  Placement = pos=(134.62,-113.263,-1.6) rot=(0.707107,-0.707107,0;3.14159rad)
FEATURE [App::Link] R4_R_0805_2012Metric_86a6360c6716_ln_006  label="R2_R_0805_2012Metric_56962076449c"
  LinkPlacement = pos=(172.974,-113.268,-1.6) rot=(0.707107,0.707107,0;3.14159rad)
  LinkedObject = -> Shape
  Placement = pos=(172.974,-113.268,-1.6) rot=(0.707107,0.707107,0;3.14159rad)
FEATURE [App::Link] R4_R_0805_2012Metric_86a6360c6716_ln_007  label="R10_R_0805_2012Metric_2acc73cfa03f"
  LinkPlacement = pos=(191.135,-106.95,-1.6) rot=(0.707107,-0.707107,0;3.14159rad)
  LinkedObject = -> Shape
  Placement = pos=(191.135,-106.95,-1.6) rot=(0.707107,-0.707107,0;3.14159rad)
FEATURE [App::Link] R4_R_0805_2012Metric_86a6360c6716_ln_008  label="R12_R_0805_2012Metric_815b7b65a8c1"
  LinkPlacement = pos=(103.886,-87.63,-1.6) rot=(1,0,0;3.14159rad)
  LinkedObject = -> Shape
  Placement = pos=(103.886,-87.63,-1.6) rot=(1,0,0;3.14159rad)
FEATURE [App::Link] C12_C_0805_2012Metric_d3958f6a5853_ln_008  label="C6_C_0805_2012Metric_cd739ad74121"
  LinkPlacement = pos=(150.601,-89.408,-1.6) rot=(1,0,0;3.14159rad)
  LinkedObject = -> Shape002
  Placement = pos=(150.601,-89.408,-1.6) rot=(1,0,0;3.14159rad)
FEATURE [App::Link] R4_R_0805_2012Metric_86a6360c6716_ln_009  label="R7_R_0805_2012Metric_250754846f0a"
  LinkPlacement = pos=(122.412,-98.552,-1.6) rot=(0,1,0;3.14159rad)
  LinkedObject = -> Shape
  Placement = pos=(122.412,-98.552,-1.6) rot=(0,1,0;3.14159rad)
FEATURE [App::Link] R4_R_0805_2012Metric_86a6360c6716_ln_010  label="R8_R_0805_2012Metric_ad0dc5043b74"
  LinkPlacement = pos=(156.845,-113.263,-1.6) rot=(0.707107,0.707107,0;3.14159rad)
  LinkedObject = -> Shape
  Placement = pos=(156.845,-113.263,-1.6) rot=(0.707107,0.707107,0;3.14159rad)
FEATURE [App::Link] R4_R_0805_2012Metric_86a6360c6716_ln_011  label="R1_R_0805_2012Metric_c1cd87a28959"
  LinkPlacement = pos=(170.434,-113.284,-1.6) rot=(0.707107,-0.707107,0;3.14159rad)
  LinkedObject = -> Shape
  Placement = pos=(170.434,-113.284,-1.6) rot=(0.707107,-0.707107,0;3.14159rad)
FEATURE [Part::Feature] Shape014  label="U2_ATMEGA328P-AU_21a7fa9f7ab9"
  Placement = pos=(146.05,-96.266,-2.3) rot=(-0.57735,0.57735,-0.57735;2.0944rad)
  shape: bbox 9 x 9 x 1.2 mm, 474 faces, 33 solids (baked)
FEATURE [App::Link] R4_R_0805_2012Metric_86a6360c6716_ln_012  label="R15_R_0805_2012Metric_f60d8f3afff3"
  LinkPlacement = pos=(154.178,-100.584,-1.6) rot=(1,0,0;3.14159rad)
  LinkedObject = -> Shape
  Placement = pos=(154.178,-100.584,-1.6) rot=(1,0,0;3.14159rad)
FEATURE [Part::Feature] Shape015  label="Y1_Crystal_HC49-4H_Vertical_bb80b93242de"
  Placement = pos=(151.13,-85.344,-1.6) rot=(0,1,0;3.14159rad)
  shape: bbox 11.05 x 4.65 x 7 mm, 26 faces (baked)
FEATURE [App::Link] R4_R_0805_2012Metric_86a6360c6716_ln_013  label="R11_R_0805_2012Metric_53982b2a4348"
  LinkPlacement = pos=(188.325,-87.63,-1.6) rot=(0,1,0;3.14159rad)
  LinkedObject = -> Shape
  Placement = pos=(188.325,-87.63,-1.6) rot=(0,1,0;3.14159rad)
FEATURE [App::Link] C12_C_0805_2012Metric_d3958f6a5853_ln_009  label="C5_C_0805_2012Metric_b3ef4e00b09e"
  LinkPlacement = pos=(146.558,-89.408,-1.6) rot=(0,1,0;3.14159rad)
  LinkedObject = -> Shape002
  Placement = pos=(146.558,-89.408,-1.6) rot=(0,1,0;3.14159rad)
FEATURE [Part::Feature] Shape016  label="J6_PinHeader_1x08_P254mm_Vertical_30cee0097060"
  Placement = pos=(137.16,-103.505,-1.6) rot=(0.707107,-0.707107,0;3.14159rad)
  shape: bbox 20.32 x 2.54 x 11.54 mm, 196 faces (baked)
FEATURE [Part::Feature] Part__Feature042  label="pcb"
  shape: bbox 20.5 x 16 x 3 mm, 296 faces, 29 solids (baked)
FEATURE [App::Part] MPU_6050_v3  label="J6_MPU 6050 v3_30cee0097060[2]"
  Group = -> [Part__Feature042]
  Origin = -> Origin017
  Placement = pos=(146.16,-110.505,-5.6) rot=(1,0,0;3.14159rad)
FEATURE [App::Link] C12_C_0805_2012Metric_d3958f6a5853_ln_010  label="C9_C_0805_2012Metric_069a42647e05"
  LinkPlacement = pos=(151.13,-113.263,-1.6) rot=(0.707107,-0.707107,0;3.14159rad)
  LinkedObject = -> Shape002
  Placement = pos=(151.13,-113.263,-1.6) rot=(0.707107,-0.707107,0;3.14159rad)
FEATURE [App::Part] Bot_4c2a
  Group = -> [C12_C_0805_2012Metric_d3958f6a5853_ln_007,R4_R_0805_2012Metric_86a6360c6716_ln_006,R4_R_0805_2012Metric_86a6360c6716_ln_007,R4_R_0805_2012Metric_86a6360c6716_ln_008,C12_C_0805_2012Metric_d3958f6a5853_ln_008,R4_R_0805_2012Metric_86a6360c6716_ln_009,R4_R_0805_2012Metric_86a6360c6716_ln_010,R4_R_0805_2012Metric_86a6360c6716_ln_011,Shape014,R4_R_0805_2012Metric_86a6360c6716_ln_012,Shape015,+5 more]
  Origin = -> Origin016
FEATURE [App::Part] Step_Models_4c2a
  Group = -> [Top_4c2a,Bot_4c2a]
  Origin = -> Origin014
  Placement = pos=(-96.12,118.42,0) rot=(0,0,1;0rad)
FEATURE [App::Part] Board_4c2a  label="TransmitterV1"
  Group = -> [Board_Geoms_4c2a,Step_Models_4c2a]
  Origin = -> Origin012
  Placement = pos=(26,6,15) rot=(0,0,1;0rad)
FEATURE [Sketcher::SketchObject] Sketch010
  ExternalGeometry = -> [Thickness]
  FullyConstrained = true
  MapMode = 5
  Placement = pos=(0,0,2) rot=(0,0,1;0rad)
  Support = -> [Thickness]
  sketch-geometry (4):
    g0: Circle CenterX=52 CenterY=37.5 CenterZ=0 NormalX=0 NormalY=0 NormalZ=1 AngleXU=0 Radius=2.5
    g1: Circle CenterX=92.5 CenterY=36.8 CenterZ=0 NormalX=0 NormalY=0 NormalZ=1 AngleXU=0 Radius=2.5
    g2: Circle CenterX=121 CenterY=11.2 CenterZ=0 NormalX=0 NormalY=0 NormalZ=1 AngleXU=0 Radius=2.5
    g3: Circle CenterX=31 CenterY=11.2 CenterZ=0 NormalX=0 NormalY=0 NormalZ=1 AngleXU=0 Radius=2.5
  constraints (12):
    c: Diameter(g3) = 5
    c: Equal(g3,g0)
    c: Equal(g3,g1)
    c: Equal(g3,g2)
    c: Distance(g3,g-6) = 11.2
    c: Distance(g3,g-4) = 31
    c: Distance(g2,g-6) = 11.2
    c: Distance(g2,g-5) = 29
    c: Distance(g0,g-3) = 12.5
    c: Distance(g0,g-4) = 52
    c: Distance(g1,g-3) = 13.2
    c: Distance(g1,g-5) = 57.5
FEATURE [PartDesign::Pad] Pad004
  BaseFeature = -> Thickness
  Direction = (1,1,1)
  Length = 11
  Length2 = 100
  Profile = -> Sketch010
  Type = 0
FEATURE [Sketcher::SketchObject] Sketch011
  ExternalGeometry = -> [Pad004]
  FullyConstrained = false
  MapMode = 5
  Placement = pos=(-1.1e-14,50,0) rot=(0,0.707107,0.707107;3.14159rad)
  Support = -> [Pad004]
  sketch-geometry (2):
    g0: Circle CenterX=-134.032 CenterY=16.8099 CenterZ=0 NormalX=0 NormalY=0 NormalZ=1 AngleXU=0 Radius=3.5
    g1: Circle CenterX=-15.9615 CenterY=16.8655 CenterZ=0 NormalX=0 NormalY=0 NormalZ=1 AngleXU=0 Radius=3.5
  constraints (4):
    c: Distance(g-4) = 21
    c: Distance(g-4) = 21
    c: Diameter(g0) = 7
    c: Equal(g0,g1)
FEATURE [PartDesign::Body] Body001
  Group = -> [Sketch002,Pad001,Fillet,Thickness,Sketch010,Pad004,Sketch011]
  Origin = -> Origin001
  Tip = -> Pad004
